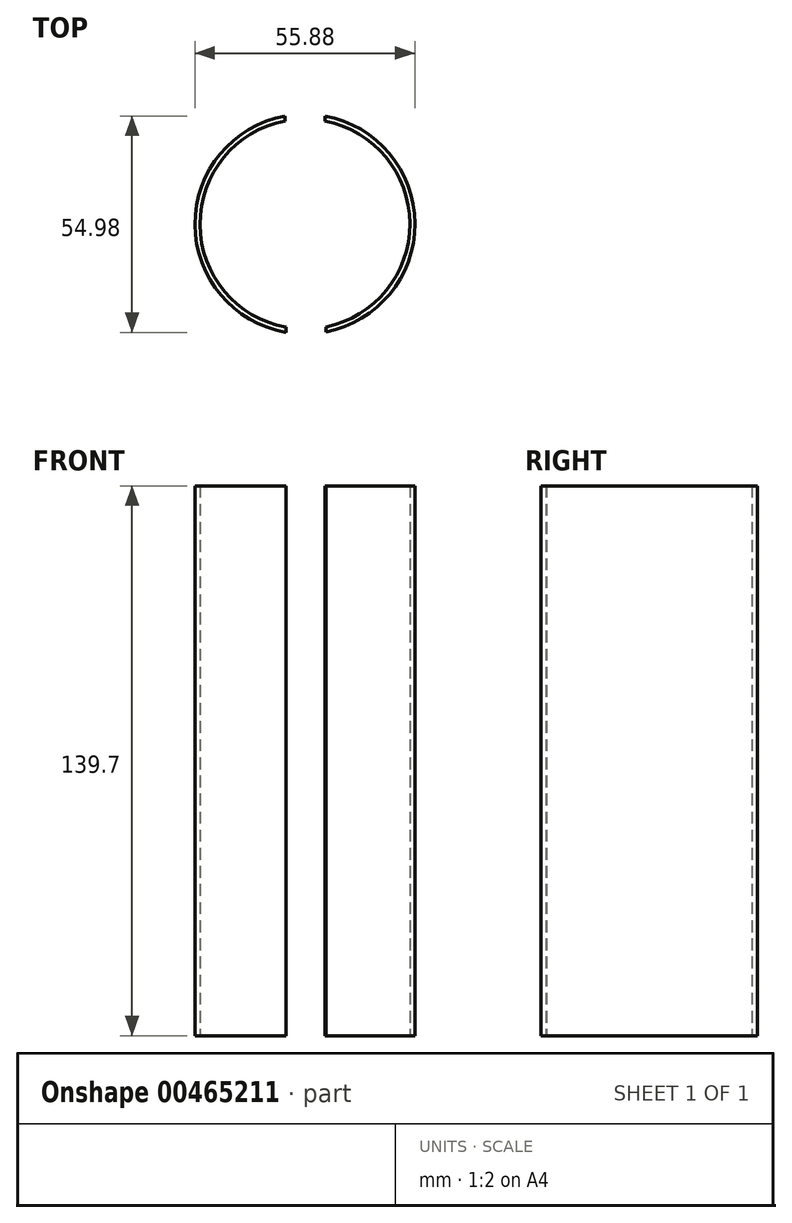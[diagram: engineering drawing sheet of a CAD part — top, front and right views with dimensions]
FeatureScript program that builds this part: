
annotation { "Feature Type Name" : "Feature", "Feature Type Description" : "" }
export const myFeature = defineFeature(function(context is Context, id is Id, definition is map)
    precondition{}
    {
        {
            var Q0;
            Q0=qCreatedBy(makeId("Top.planeOp"),FACE);
            var sketch = newSketch(context, id + "F0", { "sketchPlane" : qUnion([Q0])});
            skArc(sketch, "E0", {"start": v(-5.08, 26.18) * mm, "mid": v(-26.67, -0.11) * mm, "end": v(-4.86, -26.22) * mm});
            skArc(sketch, "E1", {"start": v(-5.08, 27.47) * mm, "mid": v(-27.94, -0.11) * mm, "end": v(-4.86, -27.51) * mm});
            skLineSegment(sketch, "E2.left", {"start": v(-4.86, -26.22) * mm, "end": v(-4.86, -27.51) * mm});
            skLineSegment(sketch, "E2.right", {"start": v(5.3, -26.14) * mm, "end": v(5.3, -27.43) * mm});
            skPoint(sketch, "E3.middle", {"position": v(0.22, -26.67) * mm});
            skPoint(sketch, "E3.middle.positionSnap0", {"position": v(0.22, -21.86) * mm});
            skPoint(sketch, "E3.centerSnap0", {"position": v(0.22, -21.86) * mm});
            skLineSegment(sketch, "E4.left", {"start": v(5.08, 26.18) * mm, "end": v(5.08, 27.47) * mm});
            skLineSegment(sketch, "E4.right", {"start": v(-5.08, 26.18) * mm, "end": v(-5.08, 27.47) * mm});
            skPoint(sketch, "E4.middle", {"position": v(0, 26.67) * mm});
            skPoint(sketch, "E5.orphan", {"position": v(5.08, 31.75) * mm});
            skPoint(sketch, "E4.bottom.start.orphan", {"position": v(5.08, 21.59) * mm});
            skPoint(sketch, "E6.orphan", {"position": v(-5.08, 21.59) * mm});
            skPoint(sketch, "E7.orphan", {"position": v(-5.08, 31.75) * mm});
            skPoint(sketch, "E8.orphan", {"position": v(-4.86, -21.86) * mm});
            skArc(sketch, "E9.trimOffspring", {"start": v(5.3, -27.43) * mm, "mid": v(27.94, 0.11) * mm, "end": v(5.08, 27.47) * mm});
            skArc(sketch, "E10.trimOffspring", {"start": v(5.3, -26.14) * mm, "mid": v(26.67, 0.11) * mm, "end": v(5.08, 26.18) * mm});
            skPoint(sketch, "E11.orphan", {"position": v(5.3, -21.86) * mm});
            skSolve(sketch);
        }
        {
            var Q0;
            Q0 = qSketchRegion(id + "F0", true);
            extrude(context, id + "F1", {"entities" : qUnion([Q0]), "depth" : 139.7 * mm});
        }
    });
